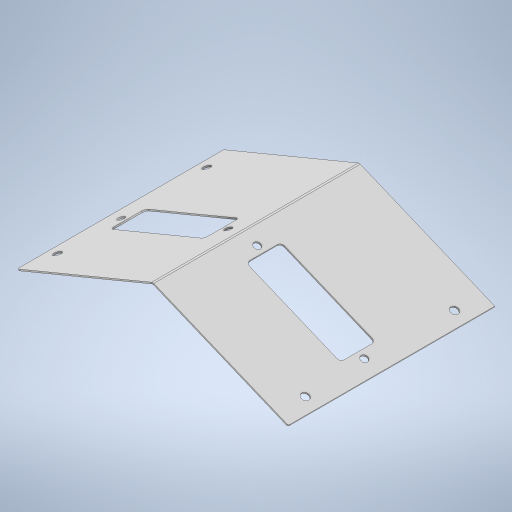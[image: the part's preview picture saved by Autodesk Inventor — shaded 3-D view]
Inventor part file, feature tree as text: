
AUTODESK INVENTOR PART (.ipt)
format: ipt  version: 2024.2 (Build 282272000, 272)  size: 459,264 bytes
history: native  units: mm
features: sketch x5, extrude x4, sheet_metal_op x3, other x3, pattern_linear x2, fillet x1, pattern_circular x1, mirror x1, chamfer x1
ambient origin geometry x8: Origin, YZ Plane, XZ Plane, XY Plane, X Axis, Y Axis, Z Axis, Center Point
bodies: Body1 (feature_tree)
feature tree (21):
  sheet_metal_op  "Contour Flange2"
  extrude  "Extrusion5"  Depth=0.9mm
  extrude  "Extrusion7"  Depth=2.0mm
  fillet  "Fillet2"  Radius=2.0mm
  pattern_circular  "Circular Pattern1"  [2 undecoded]
  pattern_linear  "Rectangular Pattern5"  Spacing1=2.0mm  [1 undecoded]
  extrude  "Extrusion8"  Depth=2.0mm
  pattern_linear  "Rectangular Pattern6"  Spacing1=8.0mm  [1 undecoded]
  mirror  "Mirror5"
  other  "Corner Chamfer1"
  chamfer  "Corner Round1"
  extrude  "Extrusion9"  Depth=2.0mm
  sketch  "Sketch1"  dims[d46=506.0mm d47=0.9mm]
  other  "Plate4"
  sheet_metal_op  "Bend4"
  sheet_metal_op  "Corner4"
  sketch  "Sketch12"  dims[d48=4.0mm d49=2.0mm d50=2.0mm]
  sketch  "Sketch14"  dims[d51=1.0mm]
  sketch  "Sketch15"  dims[d52=4.0mm]
  sketch  "Sketch16"  dims[d53=2.0mm d54=2006.0mm d55=2.0mm d56=3.0mm d57=8.0mm d58=2.0mm d59=2.0mm d115=11.0mm d116=189.129mm d117=40.75mm d118=11.0mm d119=189.129mm d120=40.75mm d121=10.0mm d122=0.0mm d131=145.0mm d132=50.0mm d133=10.0mm d134=10.0mm d135=125.0mm d136=103.139mm d137=10.0mm d138=0.0mm d139=5.0mm d140=20.0mm d141=45.0deg d143=80.0mm d145=250.0mm d146=11.0mm d147=189.129mm d148=0.0mm d149=0.0mm d150=70.0mm d152=250.0mm d153=2.0mm d154=6.0mm d155=45.0deg d156=2.0mm d159=500.0mm d160=0.0mm d161=600.0mm d162=1712.25mm]
  other  "Definition1"
note: 4 required parameter values undecoded (feature->parameter linkage not recoverable at this tier; creation-order binding heuristic only, values carry confidence <= 0.55)
